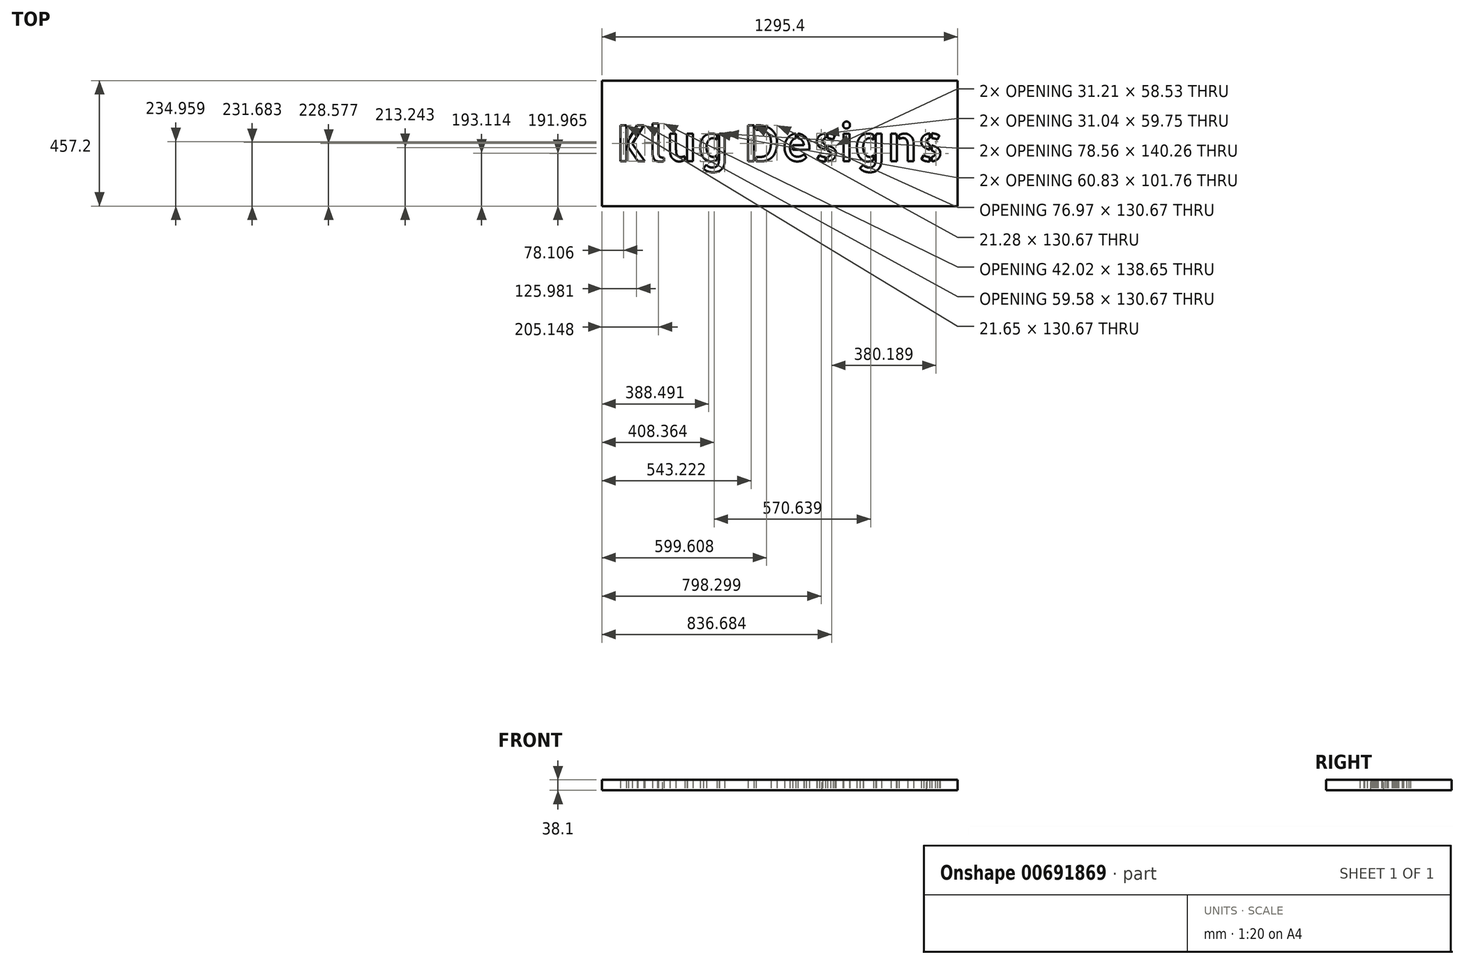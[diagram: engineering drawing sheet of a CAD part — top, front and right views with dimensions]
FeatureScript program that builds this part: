
annotation { "Feature Type Name" : "Feature", "Feature Type Description" : "" }
export const myFeature = defineFeature(function(context is Context, id is Id, definition is map)
    precondition{}
    {
        {
            var Q0;
            Q0=qCreatedBy(makeId("Top.planeOp"),FACE);
            var sketch = newSketch(context, id + "F0", { "sketchPlane" : qUnion([Q0])});
            skLineSegment(sketch, "E0.bottom", {"start": v(0, 0) * mm, "end": v(1295.4, 0) * mm});
            skLineSegment(sketch, "E0.top", {"start": v(0, 457.2) * mm, "end": v(1295.4, 457.2) * mm});
            skLineSegment(sketch, "E0.left", {"start": v(0, 0) * mm, "end": v(0, 457.2) * mm});
            skLineSegment(sketch, "E0.right", {"start": v(1295.4, 0) * mm, "end": v(1295.4, 457.2) * mm});
            skLineSegment(sketch, "E1", {"start": v(647.7, 457.2) * mm, "end": v(647.7, 0) * mm, "construction": true});
            skText(sketch, "E2", { "text": "Klug Designs", "fontName": "AllertaStencil-Regular.ttf"});
            const initialGuessF0  = {"E2": [0.0508, 0.16324, 1, 0, 0.13073]};
            skSetInitialGuess(sketch, initialGuessF0);
            skSolve(sketch);
        }
        {
            var Q0;
            Q0=makeQuery(id+"F0.imprint","IMPRINT",FACE,{"disambiguationData":[TD([[makeQuery(id+"F0.imprint","IMPRINT",EDGE,{"derivedFrom":sQuery(id+"F0.wireOp",EDGE,"E0.bottom")}),1.0]])]});
            extrude(context, id + "F1", {"entities" : qUnion([Q0]), "depth" : 38.1 * mm, "offsetDistance" : 25.4 * mm});
        }
    });
